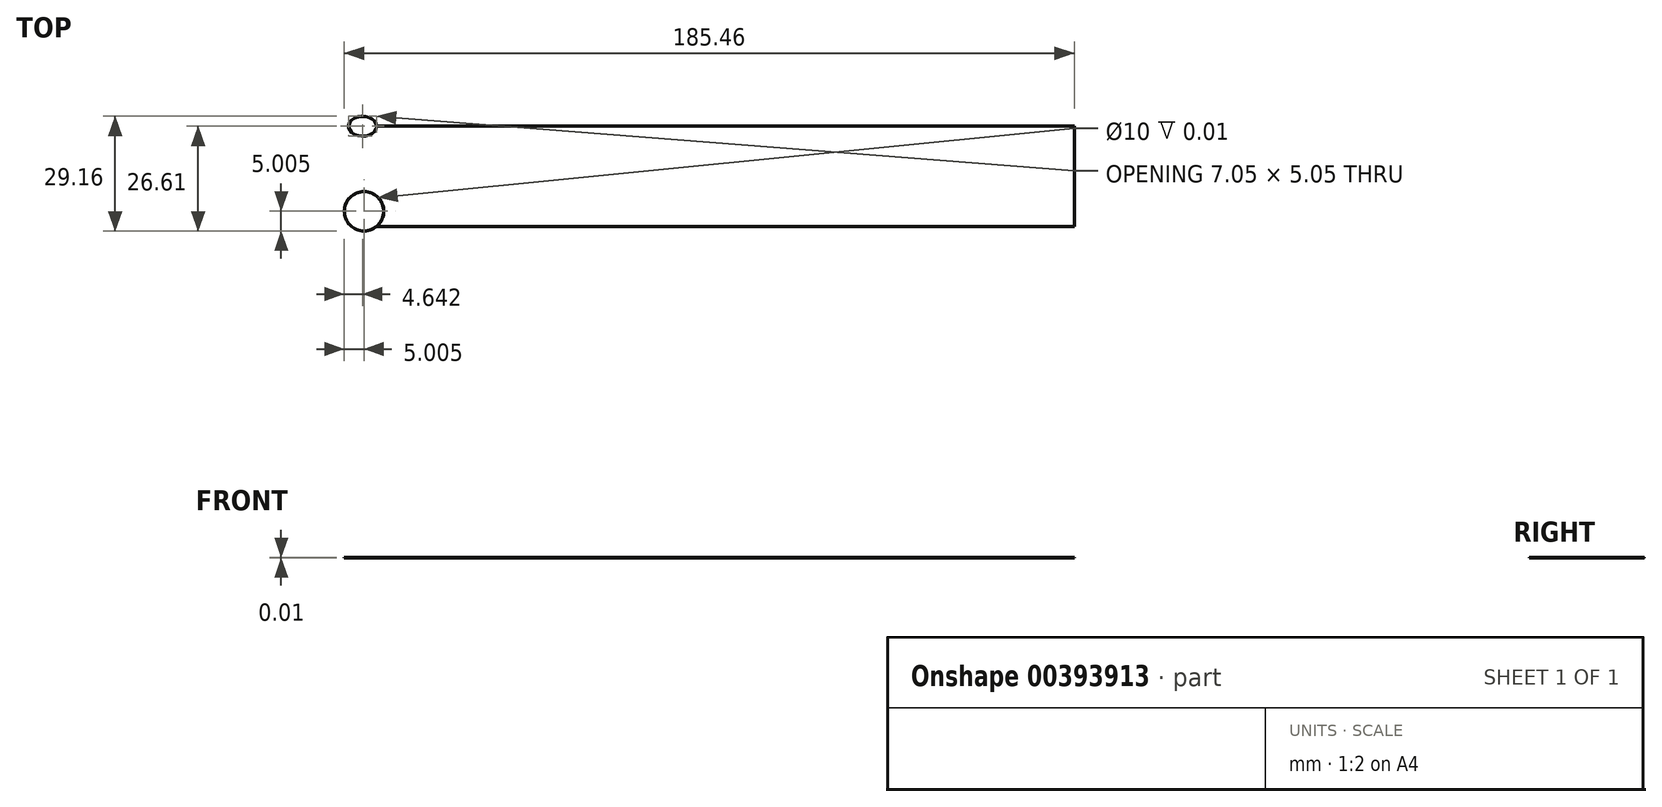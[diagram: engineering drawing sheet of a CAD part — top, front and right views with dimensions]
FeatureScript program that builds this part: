
annotation { "Feature Type Name" : "Feature", "Feature Type Description" : "" }
export const myFeature = defineFeature(function(context is Context, id is Id, definition is map)
    precondition{}
    {
        {
            var Q0;
            Q0=qCreatedBy(makeId("Top.planeOp"),FACE);
            var sketch = newSketch(context, id + "F0", { "sketchPlane" : qUnion([Q0])});
            skLineSegment(sketch, "E0.bottom", {"start": v(88.64, 0) * mm, "end": v(-88.64, 0) * mm});
            skLineSegment(sketch, "E0.top", {"start": v(88.64, 0) * mm, "end": v(-88.64, 0) * mm});
            skLineSegment(sketch, "E0.left", {"start": v(88.64, 0) * mm, "end": v(88.64, 0) * mm});
            skLineSegment(sketch, "E0.right", {"start": v(-88.64, 0) * mm, "end": v(-88.64, 0) * mm});
            skPoint(sketch, "E0.middle", {"position": v(0, 0) * mm});
            skLineSegment(sketch, "E1.bottom", {"start": v(88.64, 0) * mm, "end": v(88.65, 0) * mm});
            skLineSegment(sketch, "E1.top", {"start": v(88.64, -25.5) * mm, "end": v(88.65, -25.5) * mm});
            skLineSegment(sketch, "E1.left", {"start": v(88.64, 0) * mm, "end": v(88.64, -25.5) * mm});
            skLineSegment(sketch, "E1.right", {"start": v(88.65, 0) * mm, "end": v(88.65, -25.5) * mm});
            skLineSegment(sketch, "E2.bottom", {"start": v(88.65, -25.5) * mm, "end": v(-88.66, -25.5) * mm});
            skLineSegment(sketch, "E2.top", {"start": v(88.65, -25.48) * mm, "end": v(-88.64, -25.49) * mm});
            skLineSegment(sketch, "E2.left", {"start": v(88.65, -25.5) * mm, "end": v(88.65, -25.48) * mm});
            skEllipse(sketch, "E3", {"center": v(-92.17, 0) * mm, "majorRadius": 3.52 * mm, "minorRadius": 2.52 * mm, "majorAxis": v(-1, 0)});
            skEllipse(sketch, "E4", {"center": v(-92.17, 0) * mm, "majorRadius": 3.55 * mm, "minorRadius": 2.55 * mm, "majorAxis": v(-1, 0)});
            skCircle(sketch, "E5", {"center": v(-91.8, -21.6) * mm, "radius": 5 * mm});
            skArc(sketch, "E6", {"start": v(-88.64, -25.48) * mm, "mid": v(-94.96, -17.72) * mm, "end": v(-88.66, -25.5) * mm});
            skSolve(sketch);
        }
        {
            var Q0;
            {var subQ0=sQuery(id+"F0.wireOp",EDGE,"E0.bottom");Q0=makeQuery(id+"F0.imprint","IMPRINT",FACE,{"disambiguationData":[TD([[makeQuery(id+"F0.imprint","IMPRINT",EDGE,{"derivedFrom":subQ0}),-1.0]])]});}
            var Q1;
            {var subQ5=sQuery(id+"F0.wireOp",EDGE,"E2.right");Q1=makeQuery(id+"F0.imprint","IMPRINT",FACE,{"disambiguationData":[TD([[makeQuery(id+"F0.imprint","IMPRINT",EDGE,{"derivedFrom":subQ5}),-1.0]])]});}
            var Q2;
            {var subQ5=sQuery(id+"F0.wireOp",EDGE,"E1.bottom");Q2=makeQuery(id+"F0.imprint","IMPRINT",FACE,{"disambiguationData":[TD([[makeQuery(id+"F0.imprint","IMPRINT",EDGE,{"derivedFrom":subQ5}),-1.0]])]});}
            var Q3;
            {var subQ5=sQuery(id+"F0.wireOp",EDGE,"E2.left");Q3=makeQuery(id+"F0.imprint","IMPRINT",FACE,{"disambiguationData":[TD([[makeQuery(id+"F0.imprint","IMPRINT",EDGE,{"derivedFrom":subQ5}),1.0]])]});}
            var Q4;
            {var subQ0=sQuery(id+"F0.wireOp",EDGE,"E4");var subQ1=sQuery(id+"F0.wireOp",EDGE,"E0.bottom");var subQ2=makeQuery(id+"F0.imprint","INTERSECT",VERTEX,{"derivedFrom":[subQ1,subQ0]});Q4=makeQuery(id+"F0.imprint","IMPRINT",FACE,{"disambiguationData":[TD([[makeQuery(id+"F0.imprint","IMPRINT",EDGE,{"disambiguationData":[TD([[subQ2,-1.0]])],"derivedFrom":subQ1}),1.0]])]});}
            var Q5;
            Q5=makeQuery(id+"F0.imprint","IMPRINT",FACE,{"disambiguationData":[TD([[makeQuery(id+"F0.imprint","IMPRINT",EDGE,{"derivedFrom":sQuery(id+"F0.wireOp",EDGE,"E5")}),-1.0]])]});
            extrude(context, id + "F1", {"entities" : qUnion([Q0, Q1, Q2, Q3, Q4, Q5]), "depth" : 0.01 * mm});
        }
    });
